# Revit family: FU_Chair_Sandler_Danielle 1-2P
name_source: partatom
category: Furniture
units: mm (PartAtom-declared; Revit-internal decimal feet)

## family parameters
Always vertical = Yes
Cut with Voids When Loaded = No
OmniClass Number = 23.40.20.00
OmniClass Title = General Furniture and Specialties
Room Calculation Point = No
Shared = No
Work Plane-Based = No

## types (1)
- Danielle 1.2P
    Default Elevation = 0 mm  [stored 0 ft]
    Depth = 645 mm  [stored 2.11614 ft]
    Description = Fully upholstered side chair with ruched detailing on a metal frame.
    Frame Finish = Metal - M2 Lacquer - Sunny Yellow RAL 1037
    Height = 930 mm  [stored 3.05118 ft]
    Manufacturer = Sandler
    Model = Danielle 1.2P
    Seat Finish = Fabric - Gravity - Sunni CPC20
    URL = https://www.sandlerseating.com
    Width = 540 mm  [stored 1.77165 ft]

note: [stored X ft] marks values corroborated as IEEE doubles in the binary element streams (Revit-internal decimal feet)

## geometry (parser evidence)
native form markers: Sweep x8
no freeform markers — native parametric forms only
